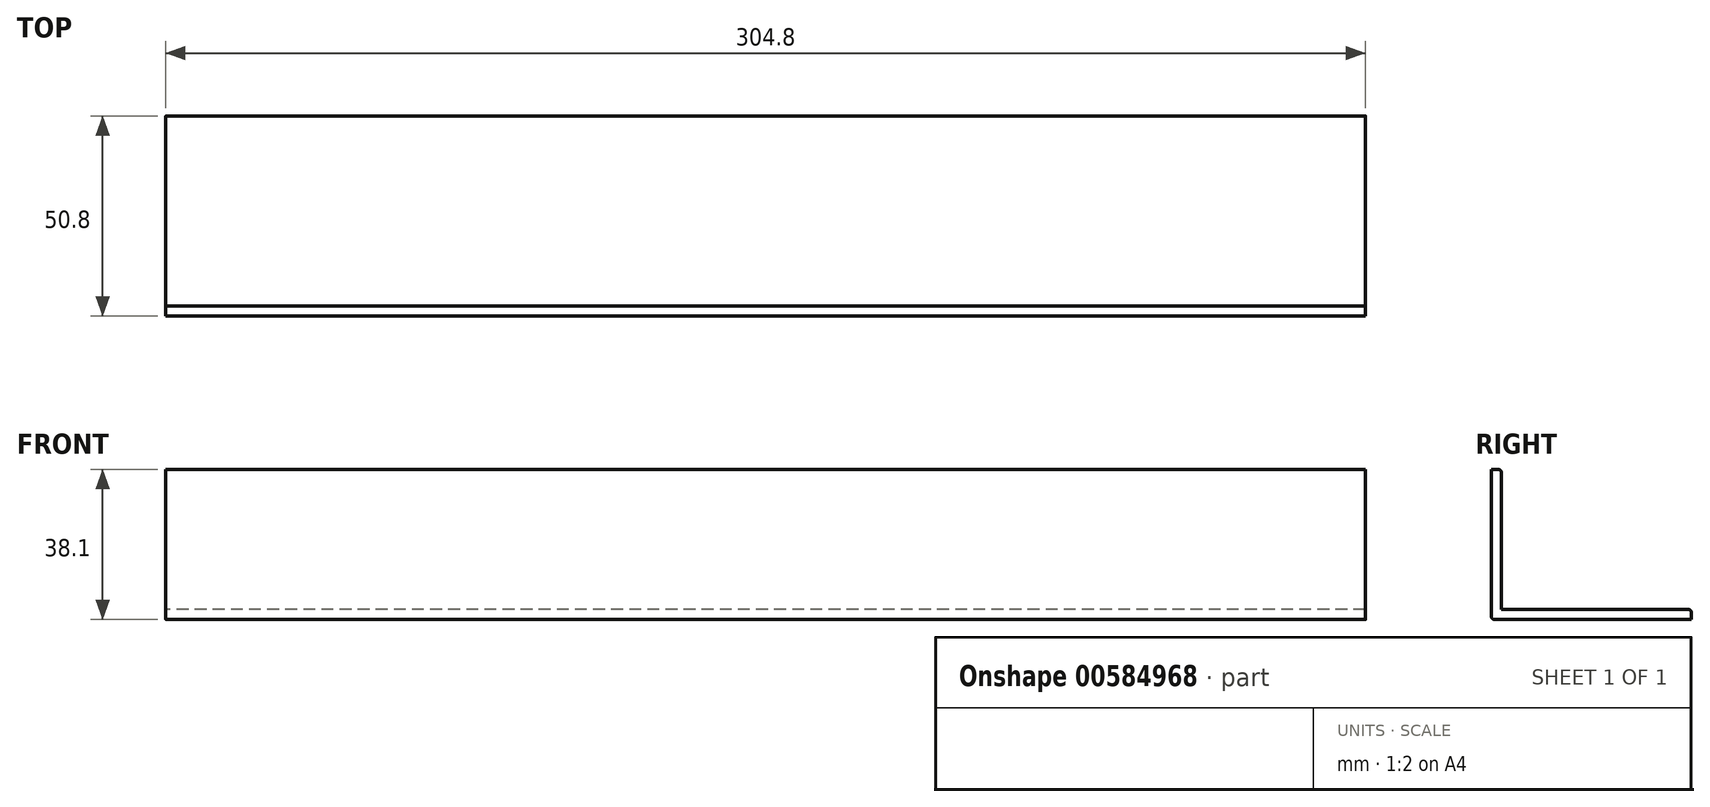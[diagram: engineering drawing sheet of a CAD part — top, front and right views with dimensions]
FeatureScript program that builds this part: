
annotation { "Feature Type Name" : "Feature", "Feature Type Description" : "" }
export const myFeature = defineFeature(function(context is Context, id is Id, definition is map)
    precondition{}
    {
        {
            var Q0;
            Q0=qCreatedBy(makeId("Right.planeOp"),FACE);
            var sketch = newSketch(context, id + "F0", { "sketchPlane" : qUnion([Q0])});
            skLineSegment(sketch, "E0", {"start": v(-16.39, 19.9) * mm, "end": v(-16.39, -17.4) * mm});
            skLineSegment(sketch, "E1", {"start": v(-15.6, -18.2) * mm, "end": v(34.41, -18.2) * mm});
            skLineSegment(sketch, "E2", {"start": v(34.41, -18.2) * mm, "end": v(34.41, -16.46) * mm});
            skLineSegment(sketch, "E3", {"start": v(33.62, -15.66) * mm, "end": v(-13.85, -15.66) * mm});
            skLineSegment(sketch, "E4", {"start": v(-13.85, -15.66) * mm, "end": v(-13.85, 19.1) * mm});
            skLineSegment(sketch, "E5", {"start": v(-14.64, 19.9) * mm, "end": v(-16.39, 19.9) * mm});
            skPoint(sketch, "E6.visualSharp", {"position": v(-13.85, 19.9) * mm});
            skArc(sketch, "E6.filletArc", {"start": v(-13.85, 19.1) * mm, "mid": v(-14.08, 19.67) * mm, "end": v(-14.64, 19.9) * mm});
            skPoint(sketch, "E7.visualSharp", {"position": v(34.41, -15.66) * mm});
            skArc(sketch, "E7.filletArc", {"start": v(34.41, -16.46) * mm, "mid": v(34.18, -15.9) * mm, "end": v(33.62, -15.66) * mm});
            skPoint(sketch, "E8.visualSharp", {"position": v(-16.39, -18.2) * mm});
            skArc(sketch, "E8.filletArc", {"start": v(-16.39, -17.4) * mm, "mid": v(-16.15, -17.97) * mm, "end": v(-15.6, -18.2) * mm});
            skSolve(sketch);
        }
        {
            var Q0;
            Q0=makeQuery(id+"F0.imprint","IMPRINT",FACE,{"disambiguationData":[TD([[makeQuery(id+"F0.imprint","IMPRINT",EDGE,{"derivedFrom":sQuery(id+"F0.wireOp",EDGE,"E0")}),1.0]])]});
            extrude(context, id + "F1", {"entities" : qUnion([Q0]), "depth" : 304.8 * mm, "offsetDistance" : 25.4 * mm});
        }
    });
